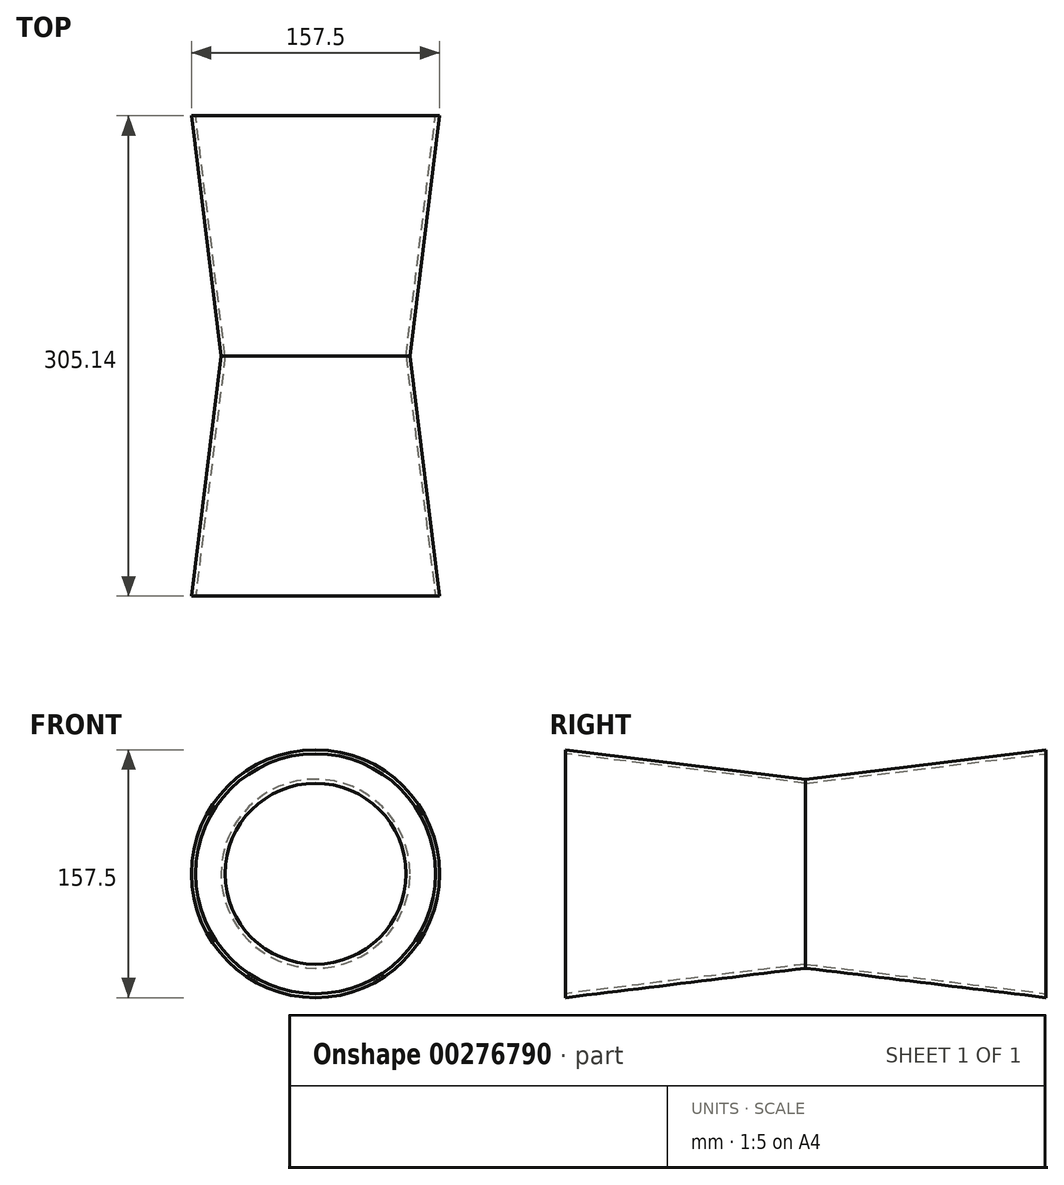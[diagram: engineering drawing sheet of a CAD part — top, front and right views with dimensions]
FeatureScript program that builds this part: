
annotation { "Feature Type Name" : "Feature", "Feature Type Description" : "" }
export const myFeature = defineFeature(function(context is Context, id is Id, definition is map)
    precondition{}
    {
        {
            var Q0;
            Q0=qCreatedBy(makeId("Front.planeOp"),FACE);
            var sketch = newSketch(context, id + "F0", { "sketchPlane" : qUnion([Q0])});
            skCircle(sketch, "E0", {"center": v(0, 0) * mm, "radius": 60.01 * mm});
            skSolve(sketch);
        }
        {
            var Q0;
            Q0=makeQuery(id+"F0.imprint","IMPRINT",FACE,{"disambiguationData":[TD([[makeQuery(id+"F0.imprint","IMPRINT",EDGE,{"derivedFrom":sQuery(id+"F0.wireOp",EDGE,"E0")}),1.0]])]});
            extrude(context, id + "F1", {"entities" : qUnion([Q0]), "endBound" : BoundingType.SYMMETRIC, "depth" : 305.14 * mm, "hasDraft" : true, "draftAngle" : 7 * degree});
        }
        {
            var Q0;
            Q0=makeQuery(id+"F1.opExtrude","CAP_FACE",FACE,{"disambiguationData":[OSD([sQuery(id+"F0.wireOp",EDGE,"E0")])],"isStart":true});
            var Q1;
            Q1=makeQuery(id+"F1.opExtrude","CAP_FACE",FACE,{"disambiguationData":[OSD([sQuery(id+"F0.wireOp",EDGE,"E0")])],"isStart":false});
            shell(context, id + "F2", {"entities" : qUnion([Q0, Q1]), "thickness" : 2.54 * mm});
        }
    });
